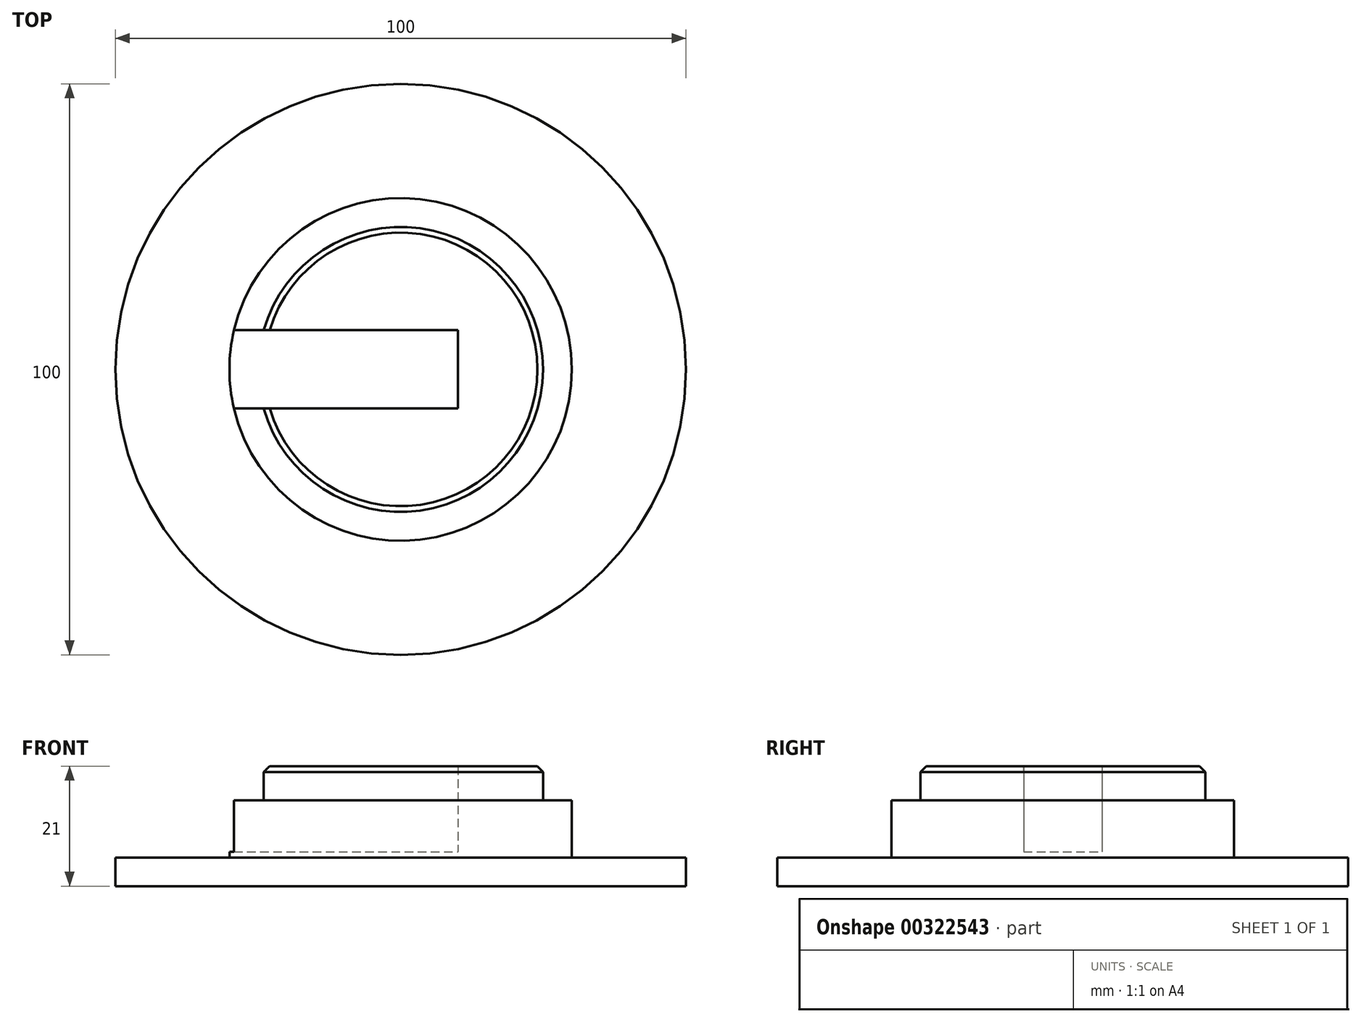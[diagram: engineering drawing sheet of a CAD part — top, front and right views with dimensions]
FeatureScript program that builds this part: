
annotation { "Feature Type Name" : "Feature", "Feature Type Description" : "" }
export const myFeature = defineFeature(function(context is Context, id is Id, definition is map)
    precondition{}
    {
        {
            var Q0;
            Q0=qCreatedBy(makeId("Top.planeOp"),FACE);
            var sketch = newSketch(context, id + "F0", { "sketchPlane" : qUnion([Q0])});
            skCircle(sketch, "E0", {"center": v(0, 0) * mm, "radius": 50 * mm});
            skSolve(sketch);
        }
        {
            var Q0;
            Q0 = qSketchRegion(id + "F0", true);
            extrude(context, id + "F1", {"entities" : qUnion([Q0]), "depth" : 5 * mm});
        }
        {
            var Q0;
            Q0=makeQuery(id+"F1.opExtrude","CAP_FACE",FACE,{"disambiguationData":[OSD([sQuery(id+"F0.wireOp",EDGE,"E0")])],"isStart":false});
            var sketch = newSketch(context, id + "F2", { "sketchPlane" : qUnion([Q0])});
            skCircle(sketch, "E1", {"center": v(0, 0) * mm, "radius": 30 * mm});
            skSolve(sketch);
        }
        {
            var Q0;
            Q0 = qSketchRegion(id + "F2", true);
            extrude(context, id + "F3", {"entities" : qUnion([Q0]), "operationType" : NewBodyOperationType.ADD, "depth" : 10 * mm});
        }
        {
            var Q0;
            Q0=makeQuery(id+"F3.opExtrude","CAP_FACE",FACE,{"disambiguationData":[OSD([sQuery(id+"F2.wireOp",EDGE,"E1")])],"isStart":false});
            var sketch = newSketch(context, id + "F4", { "sketchPlane" : qUnion([Q0])});
            skCircle(sketch, "E2", {"center": v(0, 0) * mm, "radius": 24.95 * mm});
            skSolve(sketch);
        }
        {
            var Q0;
            Q0 = qSketchRegion(id + "F4", true);
            extrude(context, id + "F5", {"entities" : qUnion([Q0]), "operationType" : NewBodyOperationType.ADD, "depth" : 6 * mm});
        }
        {
            var Q0;
            Q0=qCreatedBy(makeId("Right.planeOp"),FACE);
            var sketch = newSketch(context, id + "F6", { "sketchPlane" : qUnion([Q0])});
            skLineSegment(sketch, "E3.0", {"start": v(-24.95, 21) * mm, "end": v(24.95, 21) * mm, "construction": true});
            skLineSegment(sketch, "E4.bottom", {"start": v(-6.85, 36) * mm, "end": v(6.85, 36) * mm});
            skLineSegment(sketch, "E4.top", {"start": v(-6.85, 6) * mm, "end": v(6.85, 6) * mm});
            skLineSegment(sketch, "E4.left", {"start": v(-6.85, 36) * mm, "end": v(-6.85, 6) * mm});
            skLineSegment(sketch, "E4.right", {"start": v(6.85, 36) * mm, "end": v(6.85, 6) * mm});
            skPoint(sketch, "E4.middle", {"position": v(0, 21) * mm});
            skSolve(sketch);
        }
        {
            var Q0;
            Q0 = qSketchRegion(id + "F6", true);
            extrude(context, id + "F7", {"entities" : qUnion([Q0]), "operationType" : NewBodyOperationType.REMOVE, "oppositeDirection" : true, "depth" : 100 * mm, "hasSecondDirection" : true, "secondDirectionOppositeDirection" : false, "secondDirectionDepth" : 10 * mm});
        }
        {
            var Q0;
            Q0=makeQuery(id+"F5.opExtrude","CAP_EDGE",EDGE,{"disambiguationData":[OSD([sQuery(id+"F4.wireOp",EDGE,"E2")])],"isStart":false});
            chamfer(context, id + "F8", {"entities" : qUnion([Q0]), "width" : 1 * mm, "tangentPropagation" : true});
        }
    });
